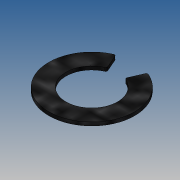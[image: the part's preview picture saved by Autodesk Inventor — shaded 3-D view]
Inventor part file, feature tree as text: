
AUTODESK INVENTOR PART (.ipt)
format: ipt  version: 2015 (Build 190159000, 159)  size: 97,792 bytes
history: native  units: mm
features: extrude x1, sketch x1
ambient origin geometry x8: Origin, YZ Plane, XZ Plane, XY Plane, X Axis, Y Axis, Z Axis, Center Point
bodies: Solid1 (feature_tree)
feature tree (2):
  extrude  "Extrusion1"  Depth=2.5mm
  sketch  "Sketch1"  dims[d0=1.5mm d1=2.5mm d2=0.1mm d3=0.2mm d4=0.0mm]
